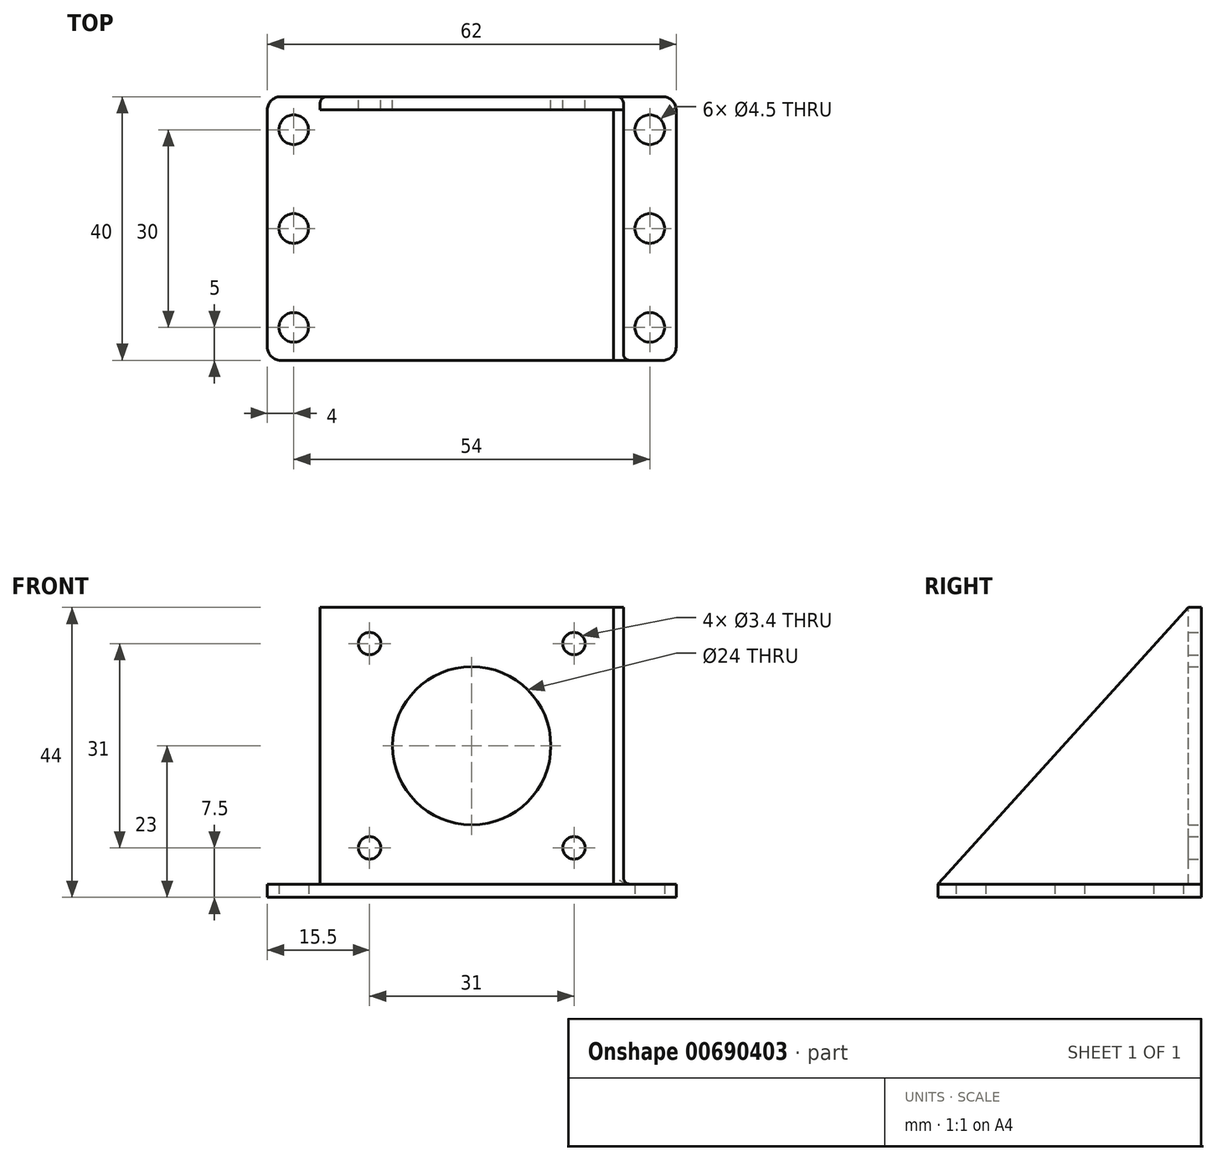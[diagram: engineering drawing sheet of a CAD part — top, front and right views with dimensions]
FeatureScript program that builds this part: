
annotation { "Feature Type Name" : "Feature", "Feature Type Description" : "" }
export const myFeature = defineFeature(function(context is Context, id is Id, definition is map)
    precondition{}
    {
        {
            var Q0;
            Q0=qCreatedBy(makeId("Top.planeOp"),FACE);
            var sketch = newSketch(context, id + "F0", { "sketchPlane" : qUnion([Q0])});
            skLineSegment(sketch, "E0.bottom", {"start": v(-31, 0) * mm, "end": v(31, 0) * mm});
            skLineSegment(sketch, "E0.top", {"start": v(-31, -40) * mm, "end": v(31, -40) * mm});
            skLineSegment(sketch, "E0.left", {"start": v(-31, 0) * mm, "end": v(-31, -40) * mm});
            skLineSegment(sketch, "E0.right", {"start": v(31, 0) * mm, "end": v(31, -40) * mm});
            skLineSegment(sketch, "E1", {"start": v(0, 0) * mm, "end": v(0, -40) * mm, "construction": true});
            skCircle(sketch, "E2", {"center": v(-27, -5) * mm, "radius": 2.25 * mm});
            skCircle(sketch, "E3", {"center": v(-27, -20) * mm, "radius": 2.25 * mm});
            skCircle(sketch, "E4", {"center": v(-27, -35) * mm, "radius": 2.25 * mm});
            skCircle(sketch, "E5.MirrorC", {"center": v(27, -35) * mm, "radius": 2.25 * mm});
            skCircle(sketch, "E6.MirrorC", {"center": v(27, -20) * mm, "radius": 2.25 * mm});
            skCircle(sketch, "E7.MirrorC", {"center": v(27, -5) * mm, "radius": 2.25 * mm});
            skSolve(sketch);
        }
        {
            var Q0;
            Q0 = qSketchRegion(id + "F0", true);
            extrude(context, id + "F1", {"entities" : qUnion([Q0]), "depth" : 2 * mm, "offsetDistance" : 25 * mm});
        }
        {
            var Q0;
            Q0=qCreatedBy(makeId("Front.planeOp"),FACE);
            var sketch = newSketch(context, id + "F2", { "sketchPlane" : qUnion([Q0])});
            skLineSegment(sketch, "E8.bottom", {"start": v(-23, 2) * mm, "end": v(23, 2) * mm});
            skLineSegment(sketch, "E8.top", {"start": v(-23, 44) * mm, "end": v(23, 44) * mm});
            skLineSegment(sketch, "E8.left", {"start": v(-23, 2) * mm, "end": v(-23, 44) * mm});
            skLineSegment(sketch, "E8.right", {"start": v(23, 2) * mm, "end": v(23, 44) * mm});
            skLineSegment(sketch, "E9", {"start": v(0, 0) * mm, "end": v(0, 44) * mm, "construction": true});
            skCircle(sketch, "E10", {"center": v(15.5, 7.5) * mm, "radius": 1.7 * mm});
            skCircle(sketch, "E11.MirrorC", {"center": v(-15.5, 7.5) * mm, "radius": 1.7 * mm});
            skLineSegment(sketch, "E12", {"start": v(-23, 23) * mm, "end": v(23, 23) * mm, "construction": true});
            skCircle(sketch, "E13", {"center": v(15.5, 38.5) * mm, "radius": 1.7 * mm});
            skCircle(sketch, "E14.MirrorC", {"center": v(-15.5, 38.5) * mm, "radius": 1.7 * mm});
            skCircle(sketch, "E15", {"center": v(0, 23) * mm, "radius": 12 * mm});
            skSolve(sketch);
        }
        {
            var Q0;
            Q0 = qSketchRegion(id + "F2", true);
            extrude(context, id + "F3", {"entities" : qUnion([Q0]), "operationType" : NewBodyOperationType.ADD, "depth" : 2 * mm, "offsetDistance" : 25 * mm});
        }
        {
            var Q0;
            Q0=makeQuery(id+"F3.opExtrude","SWEPT_FACE",FACE,{"disambiguationData":[OSD([sQuery(id+"F2.wireOp",EDGE,"E8.right")])]});
            var sketch = newSketch(context, id + "F4", { "sketchPlane" : qUnion([Q0])});
            skLineSegment(sketch, "E16", {"start": v(-2, 44) * mm, "end": v(-2, 2) * mm});
            skLineSegment(sketch, "E17", {"start": v(-2, 2) * mm, "end": v(-40, 2) * mm});
            skLineSegment(sketch, "E18", {"start": v(-40, 2) * mm, "end": v(-2, 44) * mm});
            skSolve(sketch);
        }
        {
            var Q0;
            Q0=makeQuery(id+"F4.imprint","IMPRINT",FACE,{"disambiguationData":[TD([[makeQuery(id+"F4.imprint","IMPRINT",EDGE,{"derivedFrom":sQuery(id+"F4.wireOp",EDGE,"E16")}),1.0]])]});
            extrude(context, id + "F5", {"entities" : qUnion([Q0]), "operationType" : NewBodyOperationType.ADD, "oppositeDirection" : true, "depth" : 1.5 * mm, "offsetDistance" : 25 * mm});
        }
        {
            var Q0;
            Q0=makeQuery(id+"F1.opExtrude","SWEPT_EDGE",EDGE,{"disambiguationData":[OSD([sQuery(id+"F0.wireOp",EDGE,"E0.top"),sQuery(id+"F0.wireOp",EDGE,"E0.right")])]});
            var Q1;
            Q1=makeQuery(id+"F1.opExtrude","SWEPT_EDGE",EDGE,{"disambiguationData":[OSD([sQuery(id+"F0.wireOp",EDGE,"E0.bottom"),sQuery(id+"F0.wireOp",EDGE,"E0.right")])]});
            var Q2;
            Q2=makeQuery(id+"F1.opExtrude","SWEPT_EDGE",EDGE,{"disambiguationData":[OSD([sQuery(id+"F0.wireOp",EDGE,"E0.bottom"),sQuery(id+"F0.wireOp",EDGE,"E0.left")])]});
            var Q3;
            Q3=makeQuery(id+"F1.opExtrude","SWEPT_EDGE",EDGE,{"disambiguationData":[OSD([sQuery(id+"F0.wireOp",EDGE,"E0.top"),sQuery(id+"F0.wireOp",EDGE,"E0.left")])]});
            fillet(context, id + "F6", {"entities" : qUnion([Q0, Q1, Q2, Q3]), "radius" : 2 * mm, "tangentPropagation" : true, "allowEdgeOverflow" : false});
        }
        {
            var Q0;
            Q0=makeQuery(id+"F3.opExtrude","CAP_EDGE",EDGE,{"disambiguationData":[OSD([sQuery(id+"F2.wireOp",EDGE,"E8.left")])],"isStart":true});
            var Q1;
            Q1=makeQuery(id+"F3.opExtrude","CAP_EDGE",EDGE,{"disambiguationData":[OSD([sQuery(id+"F2.wireOp",EDGE,"E8.right")])],"isStart":true});
            fillet(context, id + "F7", {"entities" : qUnion([Q0, Q1]), "radius" : 1 * mm, "tangentPropagation" : true, "allowEdgeOverflow" : false});
        }
        {
            var Q0;
            Q0=makeQuery(id+"Fc1tOQetYHx0rj2_1.1.F5.boolean.opBoolean","MERGE",EDGE,{"derivedFrom":[makeQuery(id+"F3.opExtrude","SWEPT_EDGE",EDGE,{"disambiguationData":[OSD([sQuery(id+"F2.wireOp",EDGE,"E8.bottom"),sQuery(id+"F2.wireOp",EDGE,"E8.left")])]}),makeQuery(id+"Fc1tOQetYHx0rj2_1.1.F5.opExtrude","CAP_EDGE",EDGE,{"disambiguationData":[OSD([sQuery(id+"F4.wireOp",EDGE,"E17")])],"isStart":true})]});
            var Q1;
            Q1=makeQuery(id+"F5.boolean.opBoolean","MERGE",EDGE,{"derivedFrom":[makeQuery(id+"F3.opExtrude","SWEPT_EDGE",EDGE,{"disambiguationData":[OSD([sQuery(id+"F2.wireOp",EDGE,"E8.bottom"),sQuery(id+"F2.wireOp",EDGE,"E8.right")])]}),makeQuery(id+"F5.opExtrude","CAP_EDGE",EDGE,{"disambiguationData":[OSD([sQuery(id+"F4.wireOp",EDGE,"E17")])],"isStart":true})]});
            fillet(context, id + "F8", {"entities" : qUnion([Q0, Q1]), "radius" : 1 * mm, "tangentPropagation" : true, "allowEdgeOverflow" : false});
        }
    });
